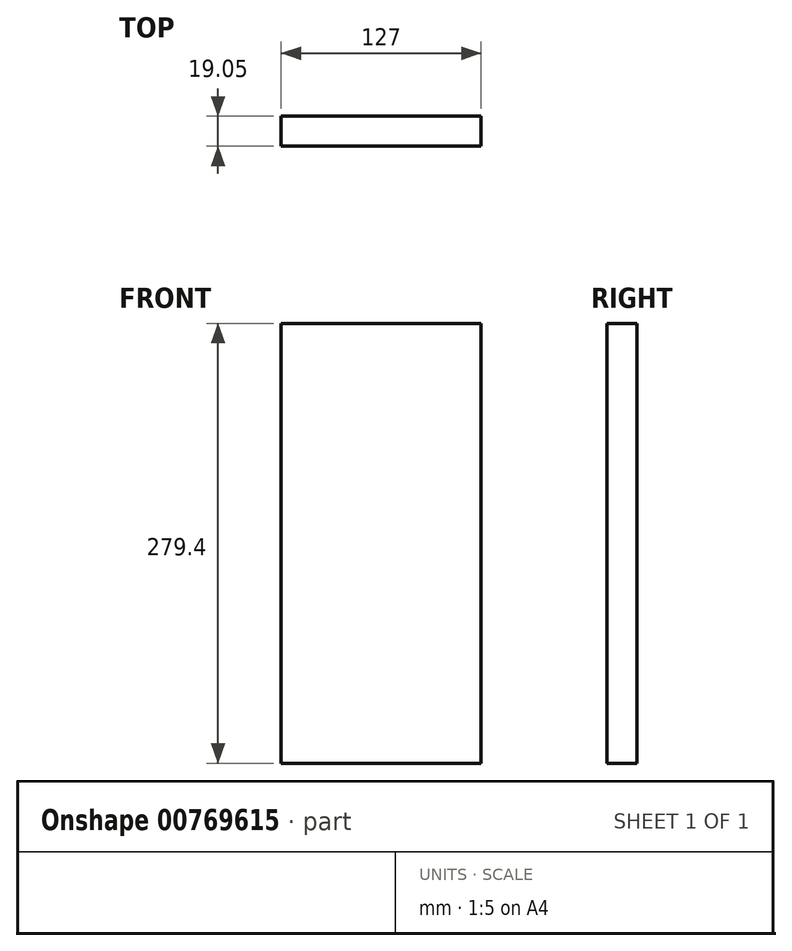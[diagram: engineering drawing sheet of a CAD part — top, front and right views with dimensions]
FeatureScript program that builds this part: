
annotation { "Feature Type Name" : "Feature", "Feature Type Description" : "" }
export const myFeature = defineFeature(function(context is Context, id is Id, definition is map)
    precondition{}
    {
        {
            var Q0;
            Q0=qCreatedBy(makeId("Front.planeOp"),FACE);
            var sketch = newSketch(context, id + "F0", { "sketchPlane" : qUnion([Q0])});
            skLineSegment(sketch, "E0.bottom", {"start": v(-61.34, 174.46) * mm, "end": v(65.66, 174.46) * mm});
            skLineSegment(sketch, "E0.top", {"start": v(-61.34, -104.94) * mm, "end": v(65.66, -104.94) * mm});
            skLineSegment(sketch, "E0.left", {"start": v(-61.34, 174.46) * mm, "end": v(-61.34, -104.94) * mm});
            skLineSegment(sketch, "E0.right", {"start": v(65.66, 174.46) * mm, "end": v(65.66, -104.94) * mm});
            skSolve(sketch);
        }
        {
            var Q0;
            Q0=makeQuery(id+"F0.imprint","IMPRINT",FACE,{"disambiguationData":[TD([[makeQuery(id+"F0.imprint","IMPRINT",EDGE,{"derivedFrom":sQuery(id+"F0.wireOp",EDGE,"E0.bottom")}),-1.0]])]});
            extrude(context, id + "F1", {"entities" : qUnion([Q0]), "depth" : 19.05 * mm, "offsetDistance" : 25.4 * mm});
        }
    });
